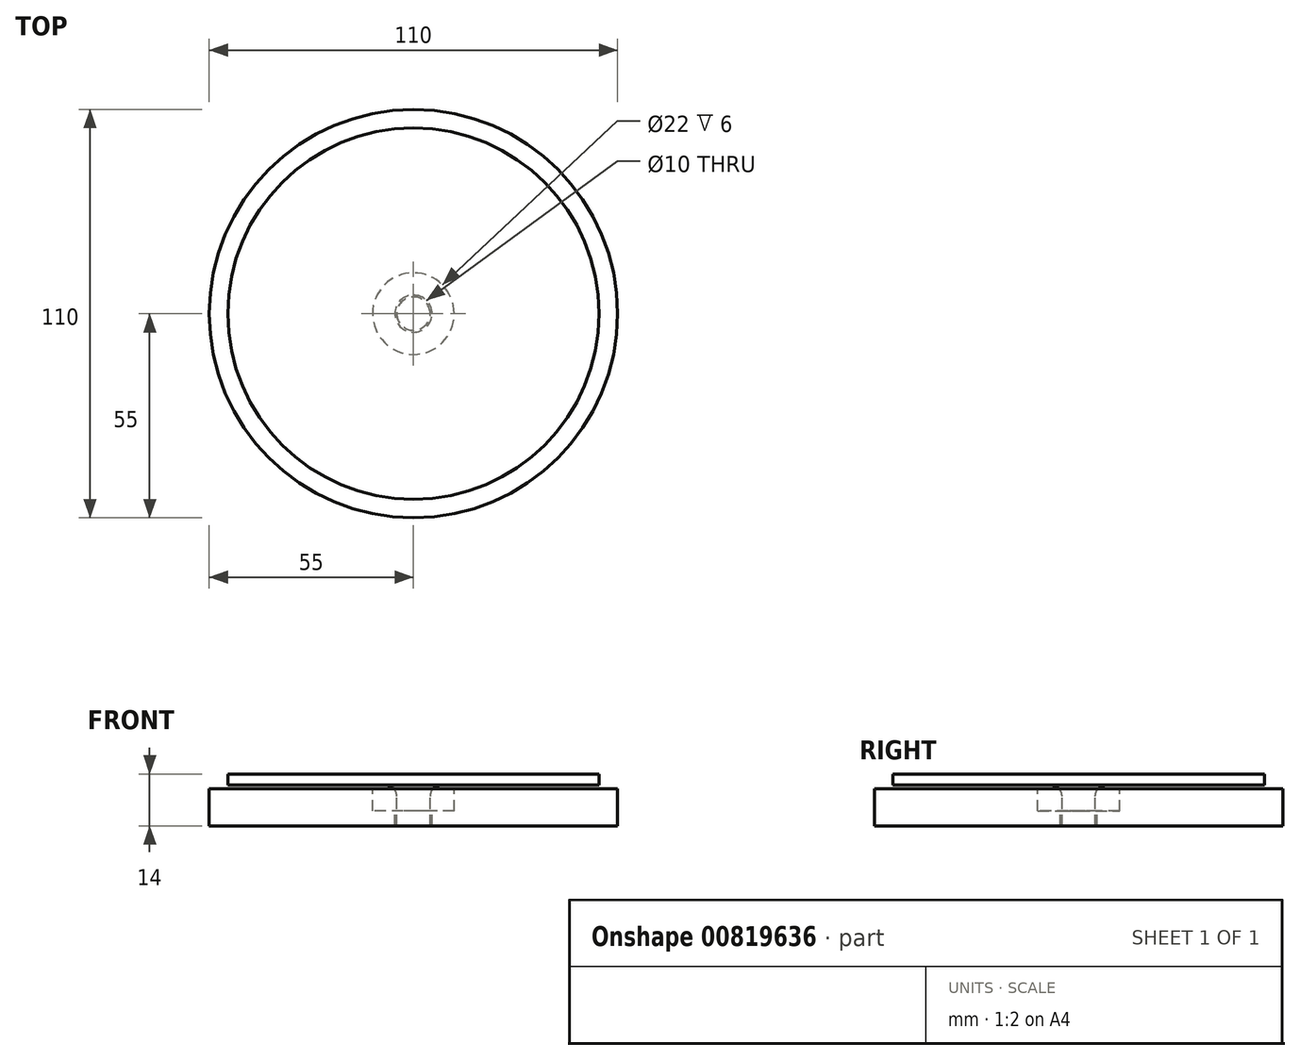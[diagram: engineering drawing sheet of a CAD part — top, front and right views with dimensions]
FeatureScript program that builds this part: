
annotation { "Feature Type Name" : "Feature", "Feature Type Description" : "" }
export const myFeature = defineFeature(function(context is Context, id is Id, definition is map)
    precondition{}
    {
        {
            var Q0;
            Q0=qCreatedBy(makeId("Front.planeOp"),FACE);
            var sketch = newSketch(context, id + "F0", { "sketchPlane" : qUnion([Q0])});
            skLineSegment(sketch, "E0.bottom", {"start": v(11, 10) * mm, "end": v(55, 10) * mm});
            skLineSegment(sketch, "E0.top", {"start": v(5, 0) * mm, "end": v(55, 0) * mm});
            skLineSegment(sketch, "E0.left", {"start": v(5, 4) * mm, "end": v(5, 0) * mm});
            skLineSegment(sketch, "E0.right", {"start": v(55, 10) * mm, "end": v(55, 0) * mm});
            skLineSegment(sketch, "E1.top", {"start": v(5, 4) * mm, "end": v(11, 4) * mm});
            skLineSegment(sketch, "E1.right", {"start": v(11, 10) * mm, "end": v(11, 4) * mm});
            skLineSegment(sketch, "E2.left", {"start": v(0, 14) * mm, "end": v(0, 0) * mm});
            skLineSegment(sketch, "E2.right", {"start": v(4.5, 11) * mm, "end": v(4.5, 0) * mm});
            skLineSegment(sketch, "E3.top", {"start": v(4.5, 11) * mm, "end": v(50, 11) * mm});
            skLineSegment(sketch, "E3.right", {"start": v(50, 14) * mm, "end": v(50, 11) * mm});
            skLineSegment(sketch, "E4", {"start": v(0, 14) * mm, "end": v(50, 14) * mm});
            skLineSegment(sketch, "E5", {"start": v(0, 0) * mm, "end": v(4.5, 0) * mm});
            skSolve(sketch);
        }
        {
            var Q0;
            Q0=makeQuery(id+"F0.imprint","IMPRINT",FACE,{"disambiguationData":[TD([[makeQuery(id+"F0.imprint","IMPRINT",EDGE,{"derivedFrom":sQuery(id+"F0.wireOp",EDGE,"E2.left")}),1.0]])]});
            var Q1;
            Q1=makeQuery(id+"F0.imprint","IMPRINT",FACE,{"disambiguationData":[TD([[makeQuery(id+"F0.imprint","IMPRINT",EDGE,{"derivedFrom":sQuery(id+"F0.wireOp",EDGE,"E0.bottom")}),-1.0]])]});
            var Q2;
            Q2=sQuery(id+"F0.wireOp",EDGE,"E2.left");
            revolve(context, id + "F1", {"surfaceOperationType" : NewSurfaceOperationType.NEW, "entities" : qUnion([Q0, Q1]), "axis" : qUnion([Q2]), "revolveType" : RevolveType.FULL});
        }
        {
            var Q0;
            Q0=makeQuery(id+"F1.opRevolve","SWEPT_EDGE",EDGE,{"disambiguationData":[OSD([sQuery(id+"F0.wireOp",EDGE,"E2.right"),sQuery(id+"F0.wireOp",EDGE,"E3.top")])]});
            fillet(context, id + "F2", {"entities" : qUnion([Q0]), "radius" : 3 * mm, "tangentPropagation" : true, "allowEdgeOverflow" : false});
        }
    });
